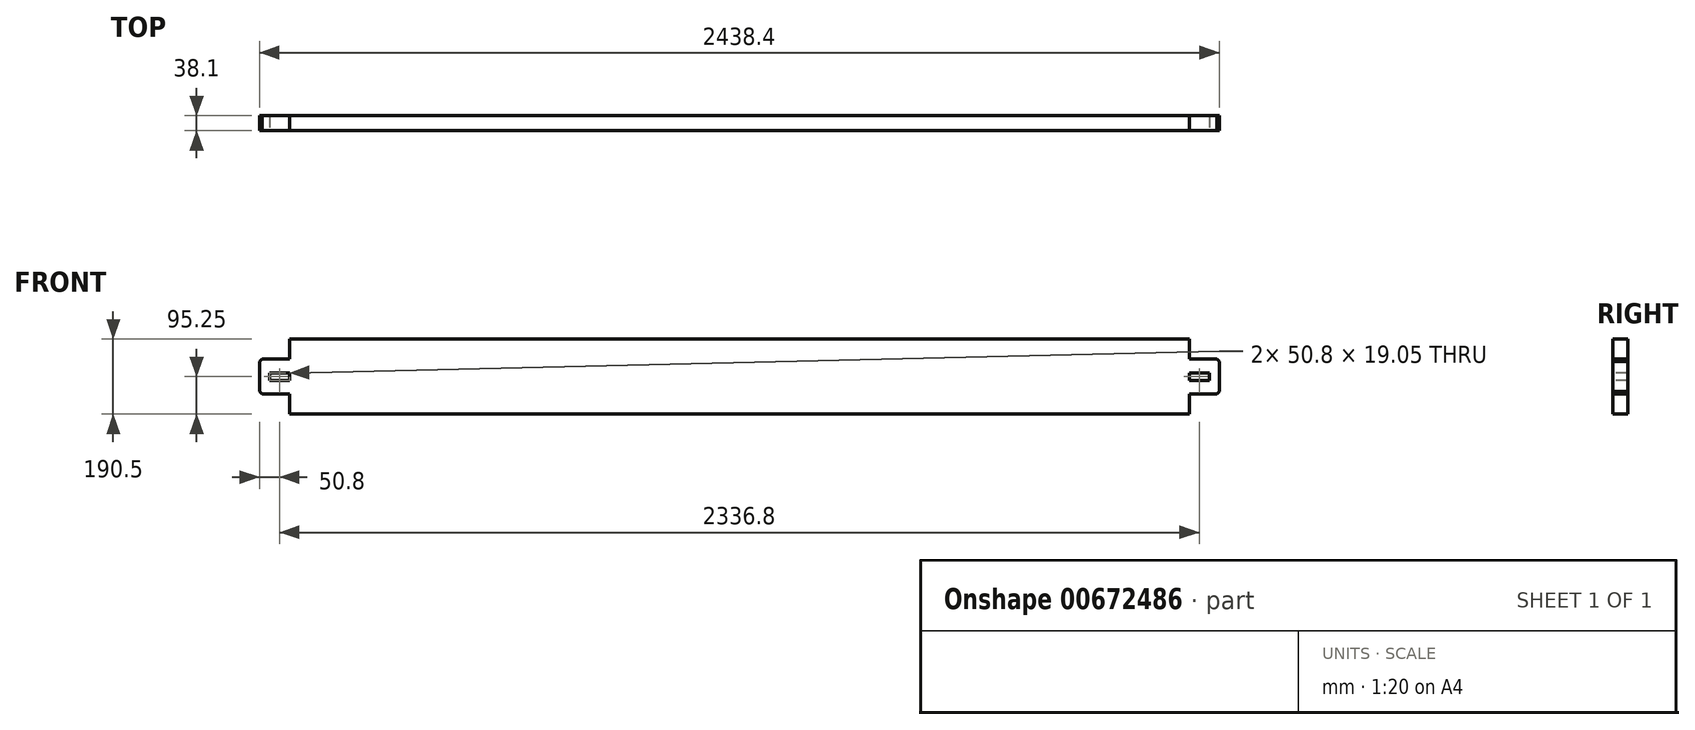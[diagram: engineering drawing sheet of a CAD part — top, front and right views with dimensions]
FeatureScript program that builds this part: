
annotation { "Feature Type Name" : "Feature", "Feature Type Description" : "" }
export const myFeature = defineFeature(function(context is Context, id is Id, definition is map)
    precondition{}
    {
        {
            var Q0;
            Q0=qCreatedBy(makeId("Front.planeOp"),FACE);
            var sketch = newSketch(context, id + "F0", { "sketchPlane" : qUnion([Q0])});
            skLineSegment(sketch, "E0.bottom", {"start": v(-1143, 95.25) * mm, "end": v(1143, 95.25) * mm});
            skLineSegment(sketch, "E0.top", {"start": v(-1143, -95.25) * mm, "end": v(1143, -95.25) * mm});
            skLineSegment(sketch, "E0.left", {"start": v(-1219.2, 44.45) * mm, "end": v(-1219.2, -44.45) * mm});
            skLineSegment(sketch, "E0.right", {"start": v(1219.2, 44.45) * mm, "end": v(1219.2, -44.45) * mm});
            skLineSegment(sketch, "E1.top", {"start": v(1219.2, 44.45) * mm, "end": v(1143, 44.45) * mm});
            skLineSegment(sketch, "E1.right", {"start": v(1143, 95.25) * mm, "end": v(1143, 44.45) * mm});
            skLineSegment(sketch, "E2.MirrorCS", {"start": v(1219.2, -44.45) * mm, "end": v(1143, -44.45) * mm});
            skLineSegment(sketch, "E3.MirrorCS", {"start": v(1143, -95.25) * mm, "end": v(1143, -44.45) * mm});
            skLineSegment(sketch, "E4.MirrorCS", {"start": v(-1219.2, -44.45) * mm, "end": v(-1143, -44.45) * mm});
            skLineSegment(sketch, "E5.MirrorCS", {"start": v(-1143, -95.25) * mm, "end": v(-1143, -44.45) * mm});
            skLineSegment(sketch, "E6.MirrorCS", {"start": v(-1219.2, 44.45) * mm, "end": v(-1143, 44.45) * mm});
            skLineSegment(sketch, "E7.MirrorCS", {"start": v(-1143, 95.25) * mm, "end": v(-1143, 44.45) * mm});
            skSolve(sketch);
        }
        {
            var Q0;
            Q0=makeQuery(id+"F0.imprint","IMPRINT",FACE,{"disambiguationData":[TD([[makeQuery(id+"F0.imprint","IMPRINT",EDGE,{"derivedFrom":sQuery(id+"F0.wireOp",EDGE,"E0.bottom")}),-1.0]])]});
            extrude(context, id + "F1", {"entities" : qUnion([Q0]), "depth" : 19.05 * mm, "offsetDistance" : 25.4 * mm, "hasSecondDirection" : true, "secondDirectionOppositeDirection" : true, "secondDirectionDepth" : 19.05 * mm});
        }
        {
            var Q0;
            Q0=makeQuery(id+"F1.opExtrude","SWEPT_EDGE",EDGE,{"disambiguationData":[OSD([sQuery(id+"F0.wireOp",EDGE,"E0.right"),sQuery(id+"F0.wireOp",EDGE,"E1.top")])]});
            var Q1;
            Q1=makeQuery(id+"F1.opExtrude","SWEPT_EDGE",EDGE,{"disambiguationData":[OSD([sQuery(id+"F0.wireOp",EDGE,"E0.right"),sQuery(id+"F0.wireOp",EDGE,"E2.MirrorCS")])]});
            var Q2;
            Q2=makeQuery(id+"F1.opExtrude","SWEPT_EDGE",EDGE,{"disambiguationData":[OSD([sQuery(id+"F0.wireOp",EDGE,"E0.left"),sQuery(id+"F0.wireOp",EDGE,"E6.MirrorCS")])]});
            var Q3;
            Q3=makeQuery(id+"F1.opExtrude","SWEPT_EDGE",EDGE,{"disambiguationData":[OSD([sQuery(id+"F0.wireOp",EDGE,"E0.left"),sQuery(id+"F0.wireOp",EDGE,"E4.MirrorCS")])]});
            chamfer(context, id + "F2", {"entities" : qUnion([Q0, Q1, Q2, Q3]), "width" : 6.35 * mm, "tangentPropagation" : true});
        }
        {
            var Q0;
            Q0=makeQuery(id+"F1.opExtrude","CAP_FACE",FACE,{"disambiguationData":[OSD([sQuery(id+"F0.wireOp",EDGE,"E0.bottom"),sQuery(id+"F0.wireOp",EDGE,"E0.top"),sQuery(id+"F0.wireOp",EDGE,"E0.left"),sQuery(id+"F0.wireOp",EDGE,"E0.right"),sQuery(id+"F0.wireOp",EDGE,"E1.top"),sQuery(id+"F0.wireOp",EDGE,"E1.right"),sQuery(id+"F0.wireOp",EDGE,"E2.MirrorCS"),sQuery(id+"F0.wireOp",EDGE,"E3.MirrorCS"),sQuery(id+"F0.wireOp",EDGE,"E4.MirrorCS"),sQuery(id+"F0.wireOp",EDGE,"E5.MirrorCS"),sQuery(id+"F0.wireOp",EDGE,"E6.MirrorCS"),sQuery(id+"F0.wireOp",EDGE,"E7.MirrorCS")])],"isStart":false});
            var sketch = newSketch(context, id + "F3", { "sketchPlane" : qUnion([Q0])});
            skLineSegment(sketch, "E8", {"start": v(1143, 44.45) * mm, "end": v(1143, -44.45) * mm, "construction": true});
            skLineSegment(sketch, "E9", {"start": v(1143, 0) * mm, "end": v(1219.2, 0) * mm, "construction": true});
            skLineSegment(sketch, "E10.bottom", {"start": v(1143, 9.53) * mm, "end": v(1193.8, 9.53) * mm});
            skLineSegment(sketch, "E10.top", {"start": v(1143, -9.52) * mm, "end": v(1193.8, -9.52) * mm});
            skLineSegment(sketch, "E10.left", {"start": v(1143, 9.53) * mm, "end": v(1143, -9.52) * mm});
            skLineSegment(sketch, "E10.right", {"start": v(1193.8, 9.53) * mm, "end": v(1193.8, -9.52) * mm});
            skPoint(sketch, "E11", {"position": v(1193.8, 0) * mm});
            skLineSegment(sketch, "E12.MirrorCS", {"start": v(-1143, 9.52) * mm, "end": v(-1193.8, 9.52) * mm});
            skLineSegment(sketch, "E13.MirrorCS", {"start": v(-1193.8, 9.53) * mm, "end": v(-1193.8, -9.52) * mm});
            skLineSegment(sketch, "E14.MirrorCS", {"start": v(-1143, -9.53) * mm, "end": v(-1193.8, -9.53) * mm});
            skLineSegment(sketch, "E15.MirrorCS", {"start": v(-1143, 9.53) * mm, "end": v(-1143, -9.52) * mm});
            skSolve(sketch);
        }
        {
            var Q0;
            Q0 = qSketchRegion(id + "F3", true);
            extrude(context, id + "F4", {"entities" : qUnion([Q0]), "operationType" : NewBodyOperationType.REMOVE, "endBound" : BoundingType.THROUGH_ALL, "oppositeDirection" : true, "depth" : 25.4 * mm, "offsetDistance" : 25.4 * mm});
        }
    });
